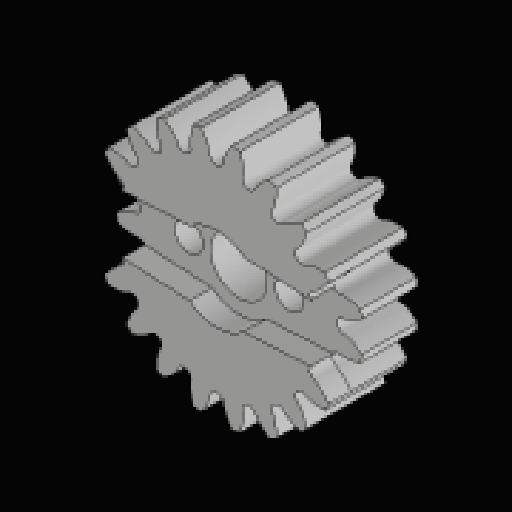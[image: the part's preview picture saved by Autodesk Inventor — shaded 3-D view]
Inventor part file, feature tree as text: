
AUTODESK INVENTOR PART (.ipt)
format: ipt  version: 2023.2 (Build 272271030, 271C)  size: 800,256 bytes
history: native  units: mm
features: reference x6, sketch x5, extrude x3, hole x2, projected_geometry x2, other x2, pattern_circular x1, revolve x1
ambient origin geometry x8: Origin, YZ Plane, XZ Plane, XY Plane, X Axis, Y Axis, Z Axis, Center Point
bodies: Solid1 (feature_tree)
feature tree (22):
  sketch  "Sketch1"  dims[d0=5.0mm d1=0.0mm]
  extrude  "Extrusion1"  TaperAngle=0.0deg  [1 undecoded]
  extrude  "Extrusion2"  Depth=200.0mm TaperAngle=360.0deg
  pattern_circular  "Circular Pattern1"  [2 undecoded]
  hole  "Hole1"  [1 undecoded]
  hole  "Hole2"  [1 undecoded]
  extrude  "Extrusion3"  Depth=0.25mm
  revolve  "Revolution2"  [1 undecoded]
  sketch  "Sketch2"  dims[d2=0.0mm d3=0.0mm d4=200.0mm d5=360.0deg]
  sketch  "Sketch3"  dims[d7=8.9mm]
  sketch  "Sketch4"  dims[d8=2.5mm d9=6.0mm d10=6.0mm d11=2.0mm d12=90.0deg d13=8.0mm d14=20.594885mm]
  reference  "Reference1"
  reference  "Reference2"
  reference  "Reference3"
  reference  "Reference4"
  reference  "Reference5"
  reference  "Reference6"
  projected_geometry  "Projected Loop1"
  sketch  "Sketch6"  dims[d15=5.0mm d16=6.0mm d17=6.0mm d18=2.0mm d19=90.0deg d20=8.0mm d21=20.594885mm d22=7.5mm d23=0.25mm d24=0.25mm d25=0.25mm d26=0.25mm d27=13.0mm d28=2.0mm d29=0.0mm d33=11.0mm d34=0.5mm d35=0.5mm d36=90.0deg]
  projected_geometry  "Projected Loop2"
  other  "Horizontal Leg Test v3.iam"
  other  "SG90 - Micro Servo 9g - Tower Pro:2"
note: 6 required parameter values undecoded (feature->parameter linkage not recoverable at this tier; creation-order binding heuristic only, values carry confidence <= 0.55)